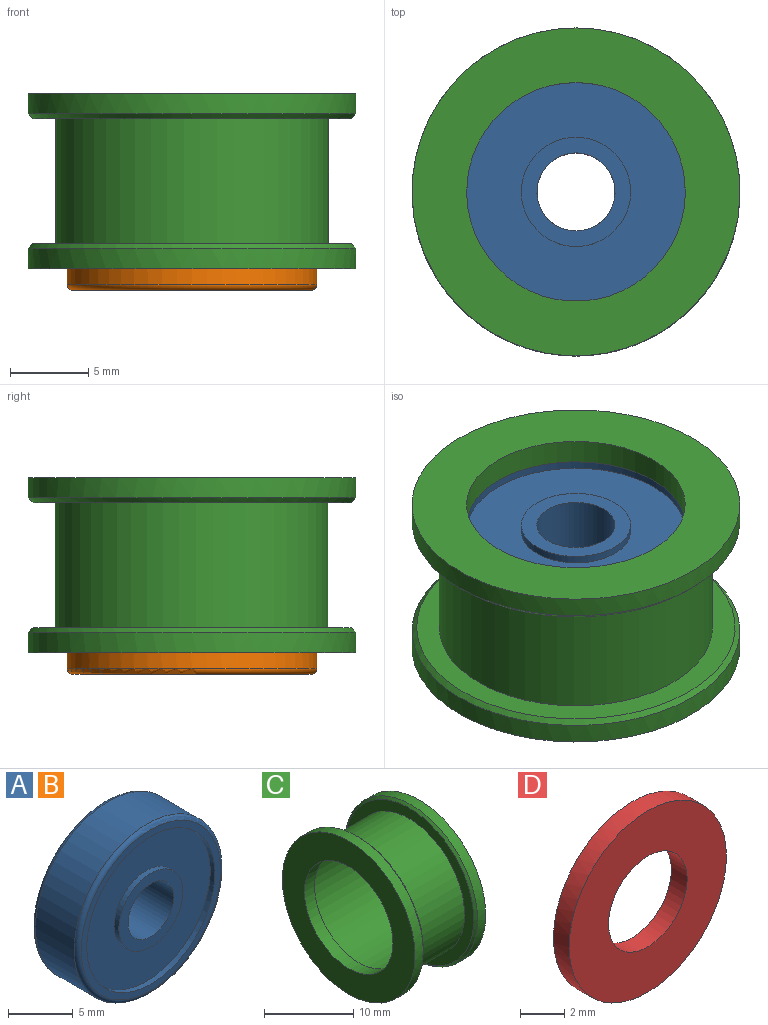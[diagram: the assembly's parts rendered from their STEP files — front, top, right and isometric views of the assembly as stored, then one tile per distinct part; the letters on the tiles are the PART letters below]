
ASSEMBLY  parts=4 mates=3
PART A: 15 faces, bbox 17.3x5x17.3 mm
  f0: torus R=7.62mm, axis (0,-1,0), area 29.9mm2, adj f1,f2
  f1: plane 15.23x15.23mm, normal (0,-1,0), area 28.2mm2, adj f0,f13
  f2: cylinder r=8mm len=16mm, axis (0,-1,0), area 212.6mm2, adj f0,f3
  f3: torus R=7.62mm, axis (0,-1,0), area 29.9mm2, adj f2,f4
  f4: plane 15.23x15.23mm, normal (0,1,0), area 28.2mm2, adj f3,f5
  f5: cylinder r=7mm len=14mm, axis (0,-1,0), area 22mm2, adj f4,f6
  f6: plane 14x14mm, normal (0,1,0), area 115.5mm2, adj f5,f7
  f7: cylinder r=3.5mm len=7mm, axis (0,-1,0), area 11mm2, adj f6,f8
  f8: plane 7x7mm, normal (0,1,0), area 18.8mm2, adj f7,f9
  f9: cylinder r=2.5mm len=5mm, axis (0,-1,0), area 78.5mm2, adj f8,f10
  f10: plane 7x7mm, normal (0,-1,0), area 18.8mm2, adj f9,f11
  f11: cylinder r=3.5mm len=7mm, axis (0,-1,0), area 11mm2, adj f10,f12
  f12: plane 14x14mm, normal (0,-1,0), area 115.5mm2, adj f11,f13
  f13: cylinder r=7mm len=14mm, axis (0,-1,0), area 22mm2, adj f1,f12
  f14: torus R=5.2mm, axis (0,-1,0), area 359.3mm2
PART B: same geometry as A
PART C: 13 faces, bbox 11.2x21x21 mm
  f0: plane 20.4x20.4mm, normal (1,0,0), area 86.3mm2, adj f1,f12
  f1: cylinder r=8.75mm len=17.5mm, axis (-1,0,0), area 439.8mm2, adj f0,f2
  f2: plane 20.4x20.4mm, normal (-1,0,0), area 86.3mm2, adj f1,f3
  f3: cone r=10.35mm half-angle=45deg, axis (1,0,0), area 27.6mm2, adj f2,f4
  f4: cylinder r=10.5mm len=21mm, axis (-1,0,0), area 85.8mm2, adj f3,f5
  f5: plane 21x21mm, normal (1,0,0), area 120.7mm2, adj f4,f6
  f6: cone r=8.22mm half-angle=45deg, axis (1,0,0), area 36.5mm2, adj f5,f7
  f7: cylinder r=7.97mm len=15.95mm, axis (-1,0,0), area 456mm2, adj f6,f8
  f8: plane 15.95x15.95mm, normal (1,0,0), area 45.9mm2, adj f7,f9
  f9: cylinder r=7mm len=14mm, axis (-1,0,0), area 70.4mm2, adj f8,f10
  f10: plane 21x21mm, normal (-1,0,0), area 192.4mm2, adj f9,f11
  f11: cylinder r=10.5mm len=21mm, axis (-1,0,0), area 85.8mm2, adj f10,f12
  f12: cone r=10.35mm half-angle=45deg, axis (-1,0,0), area 27.6mm2, adj f0,f11
PART D: 4 faces, bbox 10x1x10 mm
  f0: plane 10x10mm, normal (0,-1,0), area 58.9mm2, adj f1,f3
  f1: cylinder r=5mm len=10mm, axis (0,1,0), area 31.4mm2, adj f0,f2
  f2: plane 10x10mm, normal (0,1,0), area 58.9mm2, adj f1,f3
  f3: cylinder r=2.5mm len=5mm, axis (0,1,0), area 15.7mm2, adj f0,f2
PLACE A rot(axis=(0.58,0.58,0.58),120deg) t=(-6.7,-14.6,-13.91)mm
PLACE B rot(axis=(0.58,0.58,0.58),120deg) t=(-6.7,-14.6,-19.91)mm
PLACE C rot(axis=(0,1,0),90deg) t=(-6.7,-14.6,-15.41)mm
PLACE D rot(axis=(0.58,0.58,0.58),120deg) t=(-6.7,-14.6,-17.41)mm
MATE fastened A.f0 <-> C.f1  axis (0,0,1) through (-6.7,-14.6,-11.41)mm
MATE fastened D.f1 <-> C.f1  axis (0,0,1) through (-6.7,-14.6,-16.41)mm
MATE fastened B.f0 <-> C.f1  axis (0,0,1) through (-6.7,-14.6,-17.41)mm
